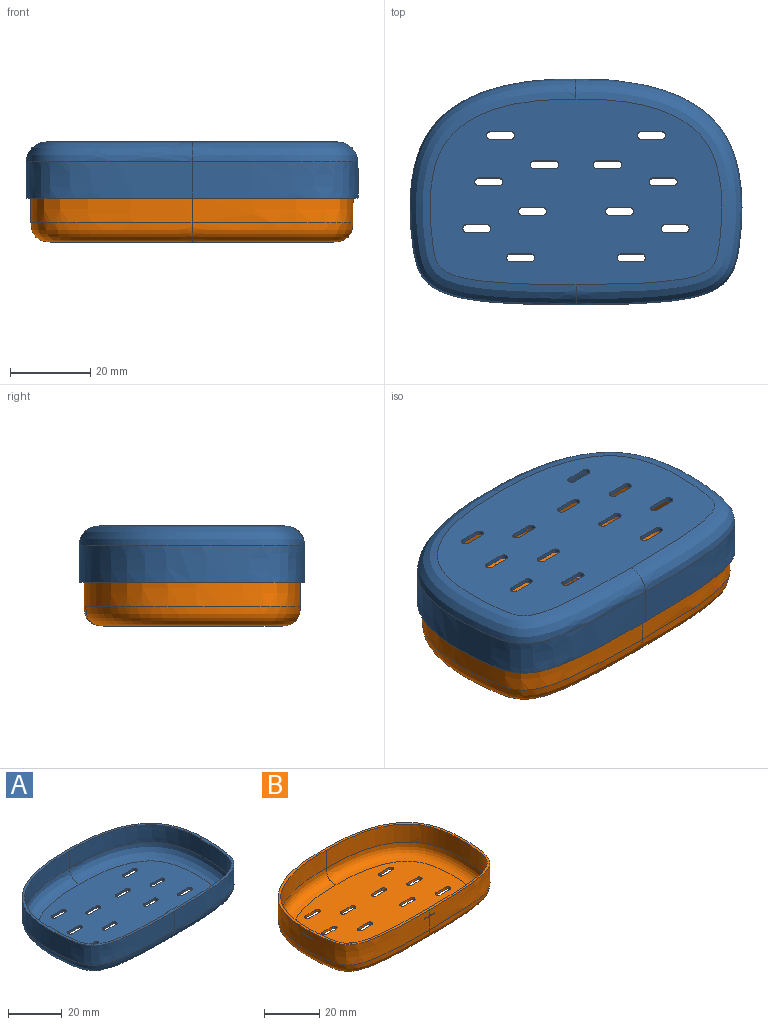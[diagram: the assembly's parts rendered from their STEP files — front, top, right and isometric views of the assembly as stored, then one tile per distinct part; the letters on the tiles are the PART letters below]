
ASSEMBLY  parts=2 mates=1
PART A: 68 faces, bbox 84x57.5x15.1 mm
  f0: extruded ~54.4x40.44mm, area 914.2mm2, adj f1,f4,f56,f62,f64,f65,f66,f67
  f1: extruded ~54.4x40.44mm, area 914.2mm2, adj f0,f4,f55,f59,f60,f61,f63,f64
  f2: plane 70.93x44.42mm, normal (0,0,1), area 2635.7mm2, adj f7,f8,f9,f10,f11,f12,f13,f14
  f3: plane 72.92x46.41mm, normal (0,0,-1), area 2837.1mm2, adj f7,f8,f9,f10,f11,f12,f13,f14
  f4: plane 84.01x57.51mm, normal (0,0,1), area 226.7mm2, adj f0,f1,f5,f6,f59,f60,f61,f62
  f5: extruded ~56.4x41.44mm, area 1061.3mm2, adj f4,f6,f58
  f6: extruded ~56.4x41.44mm, area 1061.3mm2, adj f4,f5,f57
  f7: cylinder r=1mm len=2mm, axis (0,0,1), area 3.1mm2, adj f2,f3,f8,f10
  f8: plane 5x1mm, normal (0,1,0), area 5mm2, adj f2,f3,f7,f9
  f9: cylinder r=1mm len=2mm, axis (0,0,1), area 3.1mm2, adj f2,f3,f8,f10
  f10: plane 5x1mm, normal (0,-1,0), area 5mm2, adj f2,f3,f7,f9
  f11: cylinder r=1mm len=2mm, axis (0,0,1), area 3.1mm2, adj f2,f3,f12,f14
  f12: plane 5x1mm, normal (0,-1,0), area 5mm2, adj f2,f3,f11,f13
  f13: cylinder r=1mm len=2mm, axis (0,0,1), area 3.1mm2, adj f2,f3,f12,f14
  f14: plane 5x1mm, normal (0,1,0), area 5mm2, adj f2,f3,f11,f13
  f15: plane 5x1mm, normal (0,1,0), area 5mm2, adj f2,f3,f16,f18
  f16: cylinder r=1mm len=2mm, axis (0,0,1), area 3.1mm2, adj f2,f3,f15,f17
  f17: plane 5x1mm, normal (0,-1,0), area 5mm2, adj f2,f3,f16,f18
  f18: cylinder r=1mm len=2mm, axis (0,0,1), area 3.1mm2, adj f2,f3,f15,f17
  f19: plane 5x1mm, normal (0,1,0), area 5mm2, adj f2,f3,f20,f22
  f20: cylinder r=1mm len=2mm, axis (0,0,1), area 3.1mm2, adj f2,f3,f19,f21
  f21: plane 5x1mm, normal (0,-1,0), area 5mm2, adj f2,f3,f20,f22
  f22: cylinder r=1mm len=2mm, axis (0,0,1), area 3.1mm2, adj f2,f3,f19,f21
  f23: plane 5x1mm, normal (0,-1,0), area 5mm2, adj f2,f3,f24,f26
  f24: cylinder r=1mm len=2mm, axis (0,0,1), area 3.1mm2, adj f2,f3,f23,f25
  f25: plane 5x1mm, normal (0,1,0), area 5mm2, adj f2,f3,f24,f26
  f26: cylinder r=1mm len=2mm, axis (0,0,1), area 3.1mm2, adj f2,f3,f23,f25
  f27: cylinder r=1mm len=2mm, axis (0,0,1), area 3.1mm2, adj f2,f3,f28,f30
  f28: plane 5x1mm, normal (0,-1,0), area 5mm2, adj f2,f3,f27,f29
  f29: cylinder r=1mm len=2mm, axis (0,0,1), area 3.1mm2, adj f2,f3,f28,f30
  f30: plane 5x1mm, normal (0,1,0), area 5mm2, adj f2,f3,f27,f29
  f31: cylinder r=1mm len=2mm, axis (0,0,1), area 3.1mm2, adj f2,f3,f32,f34
  f32: plane 5x1mm, normal (0,-1,0), area 5mm2, adj f2,f3,f31,f33
  f33: cylinder r=1mm len=2mm, axis (0,0,1), area 3.1mm2, adj f2,f3,f32,f34
  f34: plane 5x1mm, normal (0,1,0), area 5mm2, adj f2,f3,f31,f33
  f35: plane 5x1mm, normal (0,1,0), area 5mm2, adj f2,f3,f36,f38
  f36: cylinder r=1mm len=2mm, axis (0,0,1), area 3.1mm2, adj f2,f3,f35,f37
  f37: plane 5x1mm, normal (0,-1,0), area 5mm2, adj f2,f3,f36,f38
  f38: cylinder r=1mm len=2mm, axis (0,0,1), area 3.1mm2, adj f2,f3,f35,f37
  f39: cylinder r=1mm len=2mm, axis (0,0,1), area 3.1mm2, adj f2,f3,f40,f42
  f40: plane 5x1mm, normal (0,1,0), area 5mm2, adj f2,f3,f39,f41
  f41: cylinder r=1mm len=2mm, axis (0,0,1), area 3.1mm2, adj f2,f3,f40,f42
  f42: plane 5x1mm, normal (0,-1,0), area 5mm2, adj f2,f3,f39,f41
  f43: cylinder r=1mm len=2mm, axis (0,0,1), area 3.1mm2, adj f2,f3,f44,f46
  f44: plane 5x1mm, normal (0,1,0), area 5mm2, adj f2,f3,f43,f45
  f45: cylinder r=1mm len=2mm, axis (0,0,1), area 3.1mm2, adj f2,f3,f44,f46
  f46: plane 5x1mm, normal (0,-1,0), area 5mm2, adj f2,f3,f43,f45
  f47: plane 5x1mm, normal (0,-1,0), area 5mm2, adj f2,f3,f48,f50
  f48: cylinder r=1mm len=2mm, axis (0,0,1), area 3.1mm2, adj f2,f3,f47,f49
  f49: plane 5x1mm, normal (0,1,0), area 5mm2, adj f2,f3,f48,f50
  f50: cylinder r=1mm len=2mm, axis (0,0,1), area 3.1mm2, adj f2,f3,f47,f49
  f51: cylinder r=1mm len=2mm, axis (0,0,1), area 3.1mm2, adj f2,f3,f52,f54
  f52: plane 5x1mm, normal (0,-1,0), area 5mm2, adj f2,f3,f51,f53
  f53: cylinder r=1mm len=2mm, axis (0,0,1), area 3.1mm2, adj f2,f3,f52,f54
  f54: plane 5x1mm, normal (0,1,0), area 5mm2, adj f2,f3,f51,f53
  f55: bspline ~76.69x54.42mm, area 858.5mm2, adj f1,f2,f56
  f56: bspline ~76.69x54.42mm, area 858.5mm2, adj f0,f2,f55
  f57: bspline ~79.03x56.41mm, area 883.9mm2, adj f3,f6,f58
  f58: bspline ~79.03x56.41mm, area 883.9mm2, adj f3,f5,f57
  f59: plane 0.6x0.42mm, normal (0,-1,0), area 0.1mm2, adj f1,f4,f61
  f60: plane 0.67x0.47mm, normal (0,1,0), area 0.2mm2, adj f1,f4,f61
  f61: plane 5.15x0.87mm, normal (-0.82,0,-0.57), area 4.2mm2, adj f1,f4,f59,f60
  f62: plane 0.72x0.5mm, normal (-1,0,0), area 0.2mm2, adj f0,f4,f64
  f63: plane 0.72x0.51mm, normal (1,0,0), area 0.2mm2, adj f1,f4,f64
  f64: plane 5.01x0.73mm, normal (0,0.82,-0.57), area 4.4mm2, adj f0,f1,f4,f62,f63
  f65: plane 5.15x0.87mm, normal (0.82,0,-0.57), area 4.2mm2, adj f0,f4,f66,f67
  f66: plane 0.67x0.47mm, normal (0,1,0), area 0.2mm2, adj f0,f4,f65
  f67: plane 0.6x0.42mm, normal (0,-1,0), area 0.1mm2, adj f0,f4,f65
PART B: 71 faces, bbox 82.9x55.5x15.5 mm
  f0: extruded ~54x40.26mm, area 1027.3mm2, adj f3,f4,f10,f59,f61,f62,f67,f68
  f1: plane 72.11x45.57mm, normal (0,0,-1), area 2660.4mm2, adj f9,f10,f11,f12,f13,f14,f15,f16
  f2: plane 69.98x43.46mm, normal (0,0,1), area 2465.2mm2, adj f7,f8,f11,f12,f13,f14,f15,f16
  f3: plane 81.42x54.02mm, normal (0,0,1), area 224mm2, adj f0,f4,f5,f6
  f4: extruded ~54x40.26mm, area 1027.4mm2, adj f0,f3,f9,f59,f60,f61,f63,f64
  f5: extruded ~52x39.26mm, area 890.8mm2, adj f3,f6,f8
  f6: extruded ~52x39.26mm, area 890.8mm2, adj f3,f5,f7
  f7: bspline ~52.01x40.38mm, area 863.4mm2, adj f2,f6,f8
  f8: bspline ~52.03x39.26mm, area 865.4mm2, adj f2,f5,f7
  f9: bspline ~54.01x40.43mm, area 886.5mm2, adj f1,f4,f10
  f10: bspline ~54.03x40.26mm, area 886.8mm2, adj f0,f1,f9
  f11: cylinder r=1mm len=2mm, axis (0,0,1), area 3.1mm2, adj f1,f2,f12,f14
  f12: plane 5x1mm, normal (0,1,0), area 5mm2, adj f1,f2,f11,f13
  f13: cylinder r=1mm len=2mm, axis (0,0,1), area 3.1mm2, adj f1,f2,f12,f14
  f14: plane 5x1mm, normal (0,-1,0), area 5mm2, adj f1,f2,f11,f13
  f15: cylinder r=1mm len=2mm, axis (0,0,1), area 3.1mm2, adj f1,f2,f16,f18
  f16: plane 5x1mm, normal (0,-1,0), area 5mm2, adj f1,f2,f15,f17
  f17: cylinder r=1mm len=2mm, axis (0,0,1), area 3.1mm2, adj f1,f2,f16,f18
  f18: plane 5x1mm, normal (0,1,0), area 5mm2, adj f1,f2,f15,f17
  f19: plane 5x1mm, normal (0,1,0), area 5mm2, adj f1,f2,f20,f22
  f20: cylinder r=1mm len=2mm, axis (0,0,1), area 3.1mm2, adj f1,f2,f19,f21
  f21: plane 5x1mm, normal (0,-1,0), area 5mm2, adj f1,f2,f20,f22
  f22: cylinder r=1mm len=2mm, axis (0,0,1), area 3.1mm2, adj f1,f2,f19,f21
  f23: plane 5x1mm, normal (0,1,0), area 5mm2, adj f1,f2,f24,f26
  f24: cylinder r=1mm len=2mm, axis (0,0,1), area 3.1mm2, adj f1,f2,f23,f25
  f25: plane 5x1mm, normal (0,-1,0), area 5mm2, adj f1,f2,f24,f26
  f26: cylinder r=1mm len=2mm, axis (0,0,1), area 3.1mm2, adj f1,f2,f23,f25
  f27: plane 5x1mm, normal (0,-1,0), area 5mm2, adj f1,f2,f28,f30
  f28: cylinder r=1mm len=2mm, axis (0,0,1), area 3.1mm2, adj f1,f2,f27,f29
  f29: plane 5x1mm, normal (0,1,0), area 5mm2, adj f1,f2,f28,f30
  f30: cylinder r=1mm len=2mm, axis (0,0,1), area 3.1mm2, adj f1,f2,f27,f29
  f31: cylinder r=1mm len=2mm, axis (0,0,1), area 3.1mm2, adj f1,f2,f32,f34
  f32: plane 5x1mm, normal (0,-1,0), area 5mm2, adj f1,f2,f31,f33
  f33: cylinder r=1mm len=2mm, axis (0,0,1), area 3.1mm2, adj f1,f2,f32,f34
  f34: plane 5x1mm, normal (0,1,0), area 5mm2, adj f1,f2,f31,f33
  f35: cylinder r=1mm len=2mm, axis (0,0,1), area 3.1mm2, adj f1,f2,f36,f38
  f36: plane 5x1mm, normal (0,-1,0), area 5mm2, adj f1,f2,f35,f37
  f37: cylinder r=1mm len=2mm, axis (0,0,1), area 3.1mm2, adj f1,f2,f36,f38
  f38: plane 5x1mm, normal (0,1,0), area 5mm2, adj f1,f2,f35,f37
  f39: plane 5x1mm, normal (0,1,0), area 5mm2, adj f1,f2,f40,f42
  f40: cylinder r=1mm len=2mm, axis (0,0,1), area 3.1mm2, adj f1,f2,f39,f41
  f41: plane 5x1mm, normal (0,-1,0), area 5mm2, adj f1,f2,f40,f42
  f42: cylinder r=1mm len=2mm, axis (0,0,1), area 3.1mm2, adj f1,f2,f39,f41
  f43: cylinder r=1mm len=2mm, axis (0,0,1), area 3.1mm2, adj f1,f2,f44,f46
  f44: plane 5x1mm, normal (0,1,0), area 5mm2, adj f1,f2,f43,f45
  f45: cylinder r=1mm len=2mm, axis (0,0,1), area 3.1mm2, adj f1,f2,f44,f46
  f46: plane 5x1mm, normal (0,-1,0), area 5mm2, adj f1,f2,f43,f45
  f47: cylinder r=1mm len=2mm, axis (0,0,1), area 3.1mm2, adj f1,f2,f48,f50
  f48: plane 5x1mm, normal (0,1,0), area 5mm2, adj f1,f2,f47,f49
  f49: cylinder r=1mm len=2mm, axis (0,0,1), area 3.1mm2, adj f1,f2,f48,f50
  f50: plane 5x1mm, normal (0,-1,0), area 5mm2, adj f1,f2,f47,f49
  f51: plane 5x1mm, normal (0,-1,0), area 5mm2, adj f1,f2,f52,f54
  f52: cylinder r=1mm len=2mm, axis (0,0,1), area 3.1mm2, adj f1,f2,f51,f53
  f53: plane 5x1mm, normal (0,1,0), area 5mm2, adj f1,f2,f52,f54
  f54: cylinder r=1mm len=2mm, axis (0,0,1), area 3.1mm2, adj f1,f2,f51,f53
  f55: cylinder r=1mm len=2mm, axis (0,0,1), area 3.1mm2, adj f1,f2,f56,f58
  f56: plane 5x1mm, normal (0,-1,0), area 5mm2, adj f1,f2,f55,f57
  f57: cylinder r=1mm len=2mm, axis (0,0,1), area 3.1mm2, adj f1,f2,f56,f58
  f58: plane 5x1mm, normal (0,1,0), area 5mm2, adj f1,f2,f55,f57
  f59: plane 5.03x0.52mm, normal (0,-0.82,-0.57), area 3mm2, adj f0,f4,f60,f61,f62
  f60: plane 0.49x0.34mm, normal (1,0,0), area 0.1mm2, adj f4,f59,f61
  f61: plane 5.03x0.38mm, normal (0,0,1), area 1.7mm2, adj f0,f4,f59,f60,f62
  f62: plane 0.49x0.34mm, normal (-1,0,0), area 0.1mm2, adj f0,f59,f61
  f63: plane 5.16x0.6mm, normal (-0.82,0,-0.57), area 2.4mm2, adj f4,f64,f65,f66
  f64: plane 0.38x0.27mm, normal (0,-1,0), area 0.1mm2, adj f4,f63,f66
  f65: plane 0.31x0.22mm, normal (0,1,0), area 0mm2, adj f4,f63,f66
  f66: plane 5.08x0.37mm, normal (0,0,1), area 1.4mm2, adj f4,f63,f64,f65
  f67: plane 5.08x0.37mm, normal (0,0,1), area 1.4mm2, adj f0,f68,f69,f70
  f68: plane 5.16x0.6mm, normal (0.82,0,-0.57), area 2.4mm2, adj f0,f67,f69,f70
  f69: plane 0.38x0.27mm, normal (0,-1,0), area 0.1mm2, adj f0,f67,f68
  f70: plane 0.31x0.22mm, normal (0,1,0), area 0mm2, adj f0,f67,f68
PLACE A rot(axis=(0,1,0),180deg) t=(-6.5,65.84,23)mm
PLACE B at identity fixed
MATE slider B.f2 <-> A.f2  axis (0,0,1) through (0,12.71,0)mm
